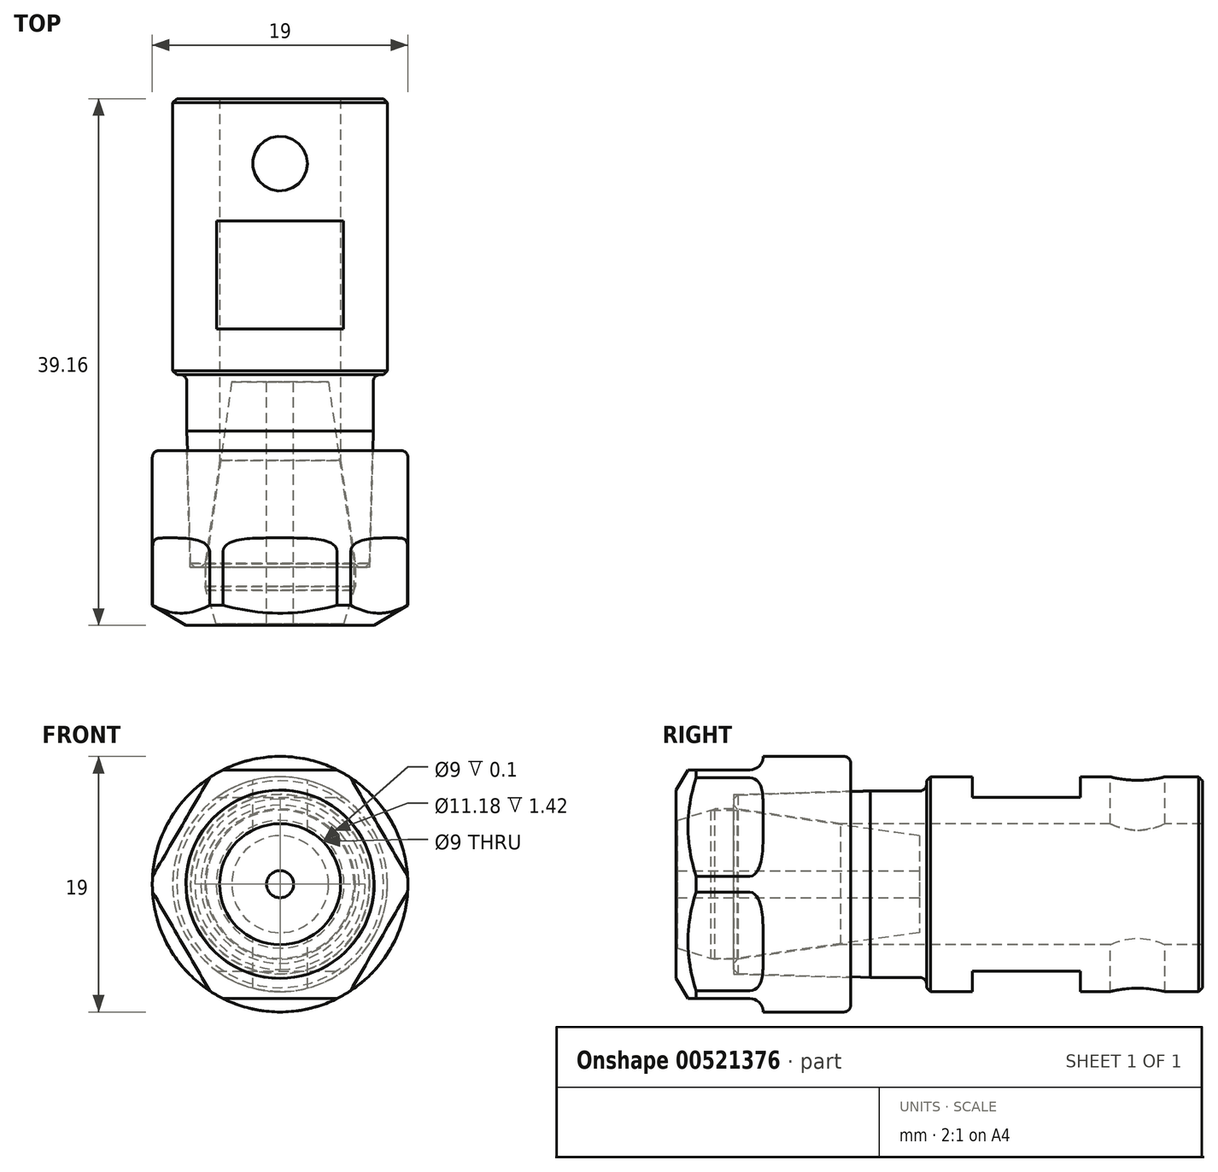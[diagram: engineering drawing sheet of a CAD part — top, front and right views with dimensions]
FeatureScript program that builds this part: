
annotation { "Feature Type Name" : "Feature", "Feature Type Description" : "" }
export const myFeature = defineFeature(function(context is Context, id is Id, definition is map)
    precondition{}
    {
        {
            var Q0;
            Q0=qCreatedBy(makeId("Right.planeOp"),FACE);
            var sketch = newSketch(context, id + "F0", { "sketchPlane" : qUnion([Q0])});
            skLineSegment(sketch, "E0", {"start": v(-34.85, 5.62) * mm, "end": v(-34.85, 6.63) * mm});
            skLineSegment(sketch, "E1", {"start": v(-24.71, 6.93) * mm, "end": v(-21.02, 6.93) * mm});
            skLineSegment(sketch, "E2", {"start": v(-20.52, 7.43) * mm, "end": v(-20.52, 7.99) * mm});
            skLineSegment(sketch, "E3", {"start": v(-20.52, 7.99) * mm, "end": v(0, 7.99) * mm});
            skLineSegment(sketch, "E4", {"start": v(0, 7.99) * mm, "end": v(0, 3.17) * mm});
            skLineSegment(sketch, "E5", {"start": v(-34.85, 0) * mm, "end": v(0, 0) * mm, "construction": true});
            skLineSegment(sketch, "E6", {"start": v(0, 3.17) * mm, "end": v(0, 0) * mm});
            skLineSegment(sketch, "E7", {"start": v(-34.85, 5.62) * mm, "end": v(-25.4, 4.29) * mm});
            skLineSegment(sketch, "E8", {"start": v(-15.62, 4.29) * mm, "end": v(-15.62, 3.17) * mm});
            skLineSegment(sketch, "E9.trimOffspring", {"start": v(-15.62, 3.17) * mm, "end": v(0, 3.17) * mm});
            skPoint(sketch, "E10.visualSharp", {"position": v(-20.52, 6.93) * mm});
            skArc(sketch, "E10.filletArc", {"start": v(-21.02, 6.93) * mm, "mid": v(-20.67, 7.08) * mm, "end": v(-20.52, 7.43) * mm});
            skLineSegment(sketch, "E11", {"start": v(-24.71, 6.93) * mm, "end": v(-34.85, 6.63) * mm});
            skPoint(sketch, "E12.orphan", {"position": v(-34.85, 6.92) * mm});
            skLineSegment(sketch, "E13", {"start": v(-25.4, 4.29) * mm, "end": v(-15.62, 4.29) * mm});
            skSolve(sketch);
        }
        {
            var Q0;
            Q0=makeQuery(id+"F0.imprint","IMPRINT",FACE,{"disambiguationData":[TD([[makeQuery(id+"F0.imprint","IMPRINT",EDGE,{"derivedFrom":sQuery(id+"F0.wireOp",EDGE,"E0")}),-1.0]])]});
            var Q1;
            Q1=makeQuery(id+"F0.imprint","IMPRINT",FACE,{"disambiguationData":[TD([[makeQuery(id+"F0.imprint","IMPRINT",EDGE,{"derivedFrom":sQuery(id+"F0.wireOp",EDGE,"E1")}),-1.0]])]});
            var Q2;
            Q2=sQuery(id+"F0.wireOp",EDGE,"E5");
            revolve(context, id + "F1", {"entities" : qUnion([Q0, Q1]), "axis" : qUnion([Q2]), "revolveType" : RevolveType.FULL});
        }
        {
            var Q0;
            Q0=makeQuery(id+"F1.opRevolve","SWEPT_EDGE",EDGE,{"disambiguationData":[OSD([sQuery(id+"F0.wireOp",EDGE,"E3"),sQuery(id+"F0.wireOp",EDGE,"E4")])]});
            var Q1;
            Q1=makeQuery(id+"F1.opRevolve","SWEPT_EDGE",EDGE,{"disambiguationData":[OSD([sQuery(id+"F0.wireOp",EDGE,"E2"),sQuery(id+"F0.wireOp",EDGE,"E3")])]});
            var Q2;
            Q2=makeQuery(id+"F1.opRevolve","SWEPT_EDGE",EDGE,{"disambiguationData":[OSD([sQuery(id+"F0.wireOp",EDGE,"E0"),sQuery(id+"F0.wireOp",EDGE,"GaHPUEVC-No4H-UHfz-TBE9-mpEbTlLyZWHn")])]});
            chamfer(context, id + "F2", {"entities" : qUnion([Q0, Q1, Q2]), "width" : .3 * mm, "tangentPropagation" : true});
        }
        {
            var Q0;
            Q0=qCreatedBy(makeId("Right.planeOp"),FACE);
            var sketch = newSketch(context, id + "F3", { "sketchPlane" : qUnion([Q0])});
            skLineSegment(sketch, "E14.bottom", {"start": v(-17.02, 9) * mm, "end": v(-9.02, 9) * mm});
            skLineSegment(sketch, "E14.top", {"start": v(-17.02, 6.5) * mm, "end": v(-9.02, 6.5) * mm});
            skLineSegment(sketch, "E14.left", {"start": v(-17.02, 9) * mm, "end": v(-17.02, 6.5) * mm});
            skLineSegment(sketch, "E14.right", {"start": v(-9.02, 9) * mm, "end": v(-9.02, 6.5) * mm});
            skLineSegment(sketch, "E15", {"start": v(-27.67, 0) * mm, "end": v(-45.97, 0) * mm, "construction": true});
            skLineSegment(sketch, "E16.MirrorCS", {"start": v(-9.02, -9) * mm, "end": v(-9.02, -6.5) * mm});
            skLineSegment(sketch, "E17.MirrorCS", {"start": v(-17.02, -9) * mm, "end": v(-17.02, -6.5) * mm});
            skLineSegment(sketch, "E18.MirrorCS", {"start": v(-17.02, -9) * mm, "end": v(-9.02, -9) * mm});
            skLineSegment(sketch, "E19.MirrorCS", {"start": v(-17.02, -6.5) * mm, "end": v(-9.02, -6.5) * mm});
            skSolve(sketch);
        }
        {
            var Q0;
            Q0=qCreatedBy(makeId("Right.planeOp"),FACE);
            var sketch = newSketch(context, id + "F4", { "sketchPlane" : qUnion([Q0])});
            skLineSegment(sketch, "E20", {"start": v(0, 0) * mm, "end": v(-26.16, 0) * mm, "construction": true});
            skLineSegment(sketch, "E21", {"start": v(-26.16, 0) * mm, "end": v(-39.16, 0) * mm});
            skLineSegment(sketch, "E22", {"start": v(-39.16, 0) * mm, "end": v(-39.16, 9.5) * mm});
            skLineSegment(sketch, "E23", {"start": v(-39.16, 9.5) * mm, "end": v(-26.16, 9.5) * mm});
            skLineSegment(sketch, "E24", {"start": v(-26.16, 9.5) * mm, "end": v(-26.16, 0) * mm});
            skLineSegment(sketch, "E25", {"start": v(-34.85, 0) * mm, "end": v(-34.85, 6.68) * mm});
            skLineSegment(sketch, "E26", {"start": v(-34.85, 6.68) * mm, "end": v(-26.16, 6.93) * mm});
            skSolve(sketch);
        }
        {
            var Q0;
            {var subQ3=sQuery(id+"F4.wireOp",EDGE,"E22");Q0=makeQuery(id+"F4.imprint","IMPRINT",FACE,{"disambiguationData":[TD([[makeQuery(id+"F4.imprint","IMPRINT",EDGE,{"derivedFrom":subQ3}),-1.0]])]});}
            var Q1;
            Q1=sQuery(id+"F4.wireOp",EDGE,"E20");
            revolve(context, id + "F5", {"entities" : qUnion([Q0]), "axis" : qUnion([Q1]), "revolveType" : RevolveType.FULL});
        }
        {
            var Q0;
            Q0=makeQuery(id+"F5.opRevolve","SWEPT_EDGE",EDGE,{"disambiguationData":[OSD([sQuery(id+"F4.wireOp",EDGE,"E23"),sQuery(id+"F4.wireOp",EDGE,"E24")])]});
            fillet(context, id + "F6", {"entities" : qUnion([Q0]), "radius" : .5 * mm, "tangentPropagation" : true, "allowEdgeOverflow" : false});
        }
        {
            var Q0;
            Q0=qCreatedBy(makeId("Right.planeOp"),FACE);
            var sketch = newSketch(context, id + "F7", { "sketchPlane" : qUnion([Q0])});
            skLineSegment(sketch, "E27", {"start": v(-39.16, 7) * mm, "end": v(-37.66, 9.5) * mm});
            skLineSegment(sketch, "E28", {"start": v(-37.66, 9.5) * mm, "end": v(-39.16, 9.5) * mm});
            skLineSegment(sketch, "E29", {"start": v(-39.16, 9.5) * mm, "end": v(-39.16, 7) * mm});
            skLineSegment(sketch, "E30", {"start": v(0, 0) * mm, "end": v(-3.44, 0) * mm});
            skLineSegment(sketch, "E31", {"start": v(-3.44, 0) * mm, "end": v(-117.43, 0) * mm, "construction": true});
            skSolve(sketch);
        }
        {
            var Q0;
            Q0=qSketchRegion(id+"F7",true);
            var Q1;
            Q1=sQuery(id+"F7.wireOp",EDGE,"E31");
            revolve(context, id + "F8", {"operationType" : NewBodyOperationType.REMOVE, "entities" : qUnion([Q0]), "axis" : qUnion([Q1]), "revolveType" : RevolveType.FULL, "oppositeDirection" : true});
        }
        {
            var Q0;
            Q0=makeQuery(id+"F5.opRevolve","SWEPT_FACE",FACE,{"disambiguationData":[OSD([sQuery(id+"F4.wireOp",EDGE,"E22")])]});
            var sketch = newSketch(context, id + "F9", { "sketchPlane" : qUnion([Q0])});
            skCircle(sketch, "E32.cCircle", {"center": v(0, 0) * mm, "radius": 8.5 * mm, "construction": true});
            skLineSegment(sketch, "E32.0", {"start": v(-4.9, 8.5) * mm, "end": v(4.9, 8.5) * mm});
            skLineSegment(sketch, "E32.1", {"start": v(4.9, 8.5) * mm, "end": v(9.81, 0) * mm});
            skLineSegment(sketch, "E32.2", {"start": v(9.81, 0) * mm, "end": v(4.9, -8.5) * mm});
            skLineSegment(sketch, "E32.3", {"start": v(4.9, -8.5) * mm, "end": v(-4.9, -8.5) * mm});
            skLineSegment(sketch, "E32.4", {"start": v(-4.9, -8.5) * mm, "end": v(-9.81, 0) * mm});
            skLineSegment(sketch, "E32.5", {"start": v(-9.81, 0) * mm, "end": v(-4.9, 8.5) * mm});
            skPoint(sketch, "E32.0.midPoint", {"position": v(0, 8.5) * mm});
            skCircle(sketch, "E33", {"center": v(0, 0) * mm, "radius": 12 * mm});
            skLineSegment(sketch, "E34", {"start": v(0, 8.5) * mm, "end": v(0, 9.5) * mm, "construction": true});
            skSolve(sketch);
        }
        {
            var Q0;
            Q0=makeQuery(id+"F9.imprint","IMPRINT",FACE,{"disambiguationData":[TD([[makeQuery(id+"F9.imprint","IMPRINT",EDGE,{"derivedFrom":sQuery(id+"F9.wireOp",EDGE,"E32.0")}),1.0]])]});
            extrude(context, id + "F10", {"entities" : qUnion([Q0]), "operationType" : NewBodyOperationType.REMOVE, "oppositeDirection" : true, "depth" : 6.5 * mm});
        }
        {
            var Q0;
            Q0=makeQuery(id+"F10.boolean.opBoolean","COPY",EDGE,{"derivedFrom":makeQuery(id+"F10.opExtrude","CAP_EDGE",EDGE,{"disambiguationData":[OSD([sQuery(id+"F9.wireOp",EDGE,"E32.0")])],"isStart":false})});
            var Q1;
            Q1=makeQuery(id+"F10.boolean.opBoolean","COPY",EDGE,{"derivedFrom":makeQuery(id+"F10.opExtrude","CAP_EDGE",EDGE,{"disambiguationData":[OSD([sQuery(id+"F9.wireOp",EDGE,"E32.1")])],"isStart":false})});
            var Q2;
            Q2=makeQuery(id+"F10.boolean.opBoolean","COPY",EDGE,{"derivedFrom":makeQuery(id+"F10.opExtrude","CAP_EDGE",EDGE,{"disambiguationData":[OSD([sQuery(id+"F9.wireOp",EDGE,"E32.2")])],"isStart":false})});
            var Q3;
            Q3=makeQuery(id+"F10.boolean.opBoolean","COPY",EDGE,{"derivedFrom":makeQuery(id+"F10.opExtrude","CAP_EDGE",EDGE,{"disambiguationData":[OSD([sQuery(id+"F9.wireOp",EDGE,"E32.3")])],"isStart":false})});
            var Q4;
            Q4=makeQuery(id+"F10.boolean.opBoolean","COPY",EDGE,{"derivedFrom":makeQuery(id+"F10.opExtrude","CAP_EDGE",EDGE,{"disambiguationData":[OSD([sQuery(id+"F9.wireOp",EDGE,"E32.4")])],"isStart":false})});
            var Q5;
            Q5=makeQuery(id+"F10.boolean.opBoolean","COPY",EDGE,{"derivedFrom":makeQuery(id+"F10.opExtrude","CAP_EDGE",EDGE,{"disambiguationData":[OSD([sQuery(id+"F9.wireOp",EDGE,"E32.5")])],"isStart":false})});
            fillet(context, id + "F11", {"entities" : qUnion([Q0, Q1, Q2, Q3, Q4, Q5]), "radius" : 1 * mm, "tangentPropagation" : true, "allowEdgeOverflow" : false});
        }
        {
            var Q0;
            Q0=makeQuery(id+"F5.opRevolve","SWEPT_FACE",FACE,{"disambiguationData":[OSD([sQuery(id+"F4.wireOp",EDGE,"E22")])]});
            var sketch = newSketch(context, id + "F12", { "sketchPlane" : qUnion([Q0])});
            skCircle(sketch, "E35", {"center": v(0, 0) * mm, "radius": 4.5 * mm});
            skSolve(sketch);
        }
        {
            var Q0;
            Q0=qSketchRegion(id+"F12",true);
            extrude(context, id + "F13", {"entities" : qUnion([Q0]), "operationType" : NewBodyOperationType.REMOVE, "endBound" : BoundingType.THROUGH_ALL, "oppositeDirection" : true, "depth" : .4 * mm});
        }
        {
            var Q0;
            Q0=qCreatedBy(makeId("Right.planeOp"),FACE);
            var sketch = newSketch(context, id + "F14", { "sketchPlane" : qUnion([Q0])});
            skLineSegment(sketch, "E36", {"start": v(-34.85, 5.59) * mm, "end": v(-34.85, 4.08) * mm});
            skLineSegment(sketch, "E37", {"start": v(-34.85, 4.08) * mm, "end": v(-39.06, 4.08) * mm});
            skLineSegment(sketch, "E38", {"start": v(-39.06, 4.08) * mm, "end": v(-39.06, 4.75) * mm});
            skLineSegment(sketch, "E39", {"start": v(0, 0) * mm, "end": v(-41.19, 0) * mm, "construction": true});
            skLineSegment(sketch, "E40", {"start": v(-39.06, 4.75) * mm, "end": v(-36.27, 5.59) * mm});
            skLineSegment(sketch, "E41", {"start": v(-36.27, 5.59) * mm, "end": v(-34.85, 5.59) * mm});
            skSolve(sketch);
        }
        {
            var Q0;
            Q0=qSketchRegion(id+"F14",true);
            var Q1;
            Q1=sQuery(id+"F14.wireOp",EDGE,"E39");
            revolve(context, id + "F15", {"operationType" : NewBodyOperationType.REMOVE, "entities" : qUnion([Q0]), "axis" : qUnion([Q1]), "revolveType" : RevolveType.FULL, "oppositeDirection" : true});
        }
        {
            var Q0;
            Q0=qCreatedBy(makeId("Right.planeOp"),FACE);
            var sketch = newSketch(context, id + "F16", { "sketchPlane" : qUnion([Q0])});
            skLineSegment(sketch, "E42", {"start": v(0, 0) * mm, "end": v(-39.06, 0) * mm, "construction": true});
            skLineSegment(sketch, "E43", {"start": v(-39.06, 1) * mm, "end": v(-39.06, 4.75) * mm});
            skLineSegment(sketch, "E44", {"start": v(-39.06, 4.75) * mm, "end": v(-36.56, 5.5) * mm});
            skLineSegment(sketch, "E45", {"start": v(-36.56, 5.5) * mm, "end": v(-34.56, 5.5) * mm});
            skLineSegment(sketch, "E46", {"start": v(-34.56, 5.5) * mm, "end": v(-21.06, 3.6) * mm});
            skLineSegment(sketch, "E47", {"start": v(-21.06, 3.6) * mm, "end": v(-21.06, 1) * mm});
            skLineSegment(sketch, "E48", {"start": v(-39.06, 1) * mm, "end": v(-21.06, 1) * mm});
            skPoint(sketch, "E49.orphan", {"position": v(-21.06, 0) * mm});
            skSolve(sketch);
        }
        {
            var Q0;
            Q0=qSketchRegion(id+"F16",true);
            var Q1;
            Q1=qConstructionFilter(qBodyType(qCreatedBy(id+"F16",EDGE),BodyType.WIRE),ConstructionObject.NO);
            var Q2;
            Q2=sQuery(id+"F16.wireOp",EDGE,"E42");
            revolve(context, id + "F17", {"entities" : qUnion([Q0]), "surfaceEntities" : qUnion([Q1]), "axis" : qUnion([Q2]), "revolveType" : RevolveType.FULL});
        }
        {
            var Q0;
            Q0=qCreatedBy(makeId("Right.planeOp"),FACE);
            var sketch = newSketch(context, id + "F18", { "sketchPlane" : qUnion([Q0])});
            skLineSegment(sketch, "E50", {"start": v(0, 0) * mm, "end": v(-36.73, 0) * mm, "construction": true});
            skLineSegment(sketch, "E51.bottom", {"start": v(-17.12, 9.1) * mm, "end": v(-9.1, 9.1) * mm});
            skLineSegment(sketch, "E51.top", {"start": v(-17.12, 6.45) * mm, "end": v(-9.1, 6.45) * mm});
            skLineSegment(sketch, "E51.left", {"start": v(-17.12, 9.1) * mm, "end": v(-17.12, 6.45) * mm});
            skLineSegment(sketch, "E51.right", {"start": v(-9.1, 9.1) * mm, "end": v(-9.1, 6.45) * mm});
            skLineSegment(sketch, "E52.MirrorCS", {"start": v(-17.12, -9.1) * mm, "end": v(-9.1, -9.1) * mm});
            skLineSegment(sketch, "E53.MirrorCS", {"start": v(-17.12, -6.45) * mm, "end": v(-9.1, -6.45) * mm});
            skLineSegment(sketch, "E54.MirrorCS", {"start": v(-9.1, -9.1) * mm, "end": v(-9.1, -6.45) * mm});
            skLineSegment(sketch, "E55.MirrorCS", {"start": v(-17.12, -9.1) * mm, "end": v(-17.12, -6.45) * mm});
            skSolve(sketch);
        }
        {
            var Q0;
            Q0=qSketchRegion(id+"F18",true);
            extrude(context, id + "F19", {"entities" : qUnion([Q0]), "operationType" : NewBodyOperationType.REMOVE, "oppositeDirection" : true, "depth" : 5.3 * mm, "hasSecondDirection" : true, "secondDirectionOppositeDirection" : false, "secondDirectionDepth" : 25 * mm});
        }
        {
            var Q0;
            Q0=qCreatedBy(makeId("Top.planeOp"),FACE);
            var sketch = newSketch(context, id + "F20", { "sketchPlane" : qUnion([Q0])});
            skLineSegment(sketch, "E56", {"start": v(0, 0) * mm, "end": v(0, 0) * mm});
            skCircle(sketch, "E57", {"center": v(0, -4.83) * mm, "radius": 2.03 * mm});
            skLineSegment(sketch, "E58", {"start": v(0, -6.86) * mm, "end": v(0, -2.8) * mm, "construction": true});
            skSolve(sketch);
        }
        {
            var Q0;
            Q0=makeQuery(id+"F20.imprint","IMPRINT",FACE,{"disambiguationData":[TD([[makeQuery(id+"F20.imprint","IMPRINT",EDGE,{"derivedFrom":sQuery(id+"F20.wireOp",EDGE,"E57")}),1.0]])]});
            extrude(context, id + "F21", {"entities" : qUnion([Q0]), "operationType" : NewBodyOperationType.REMOVE, "oppositeDirection" : true, "depth" : 9.1 * mm, "hasSecondDirection" : true, "secondDirectionOppositeDirection" : false, "secondDirectionDepth" : 25 * mm});
        }
    });
